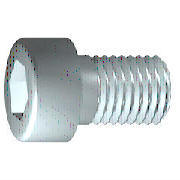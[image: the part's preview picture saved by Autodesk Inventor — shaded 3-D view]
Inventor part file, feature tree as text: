
AUTODESK INVENTOR PART (.ipt)
format: ipt  version: 2025 (Build 290162010, 162A)  size: 189,440 bytes
history: native  units: mm (DEFAULTED — no unit token found)
features: extrude x1, plane x1, fillet x1
ambient origin geometry x7: Origin, YZ Plane, XY Plane, X Axis, Y Axis, Z Axis, Center Point
bodies: Solid1 (feature_tree), Body (feature_tree)
feature tree (3):
  extrude  "Slot"  Depth=18.0mm
  plane  "Work Plane1"
  fillet  "Fillet2"  Radius=0.306825mm
